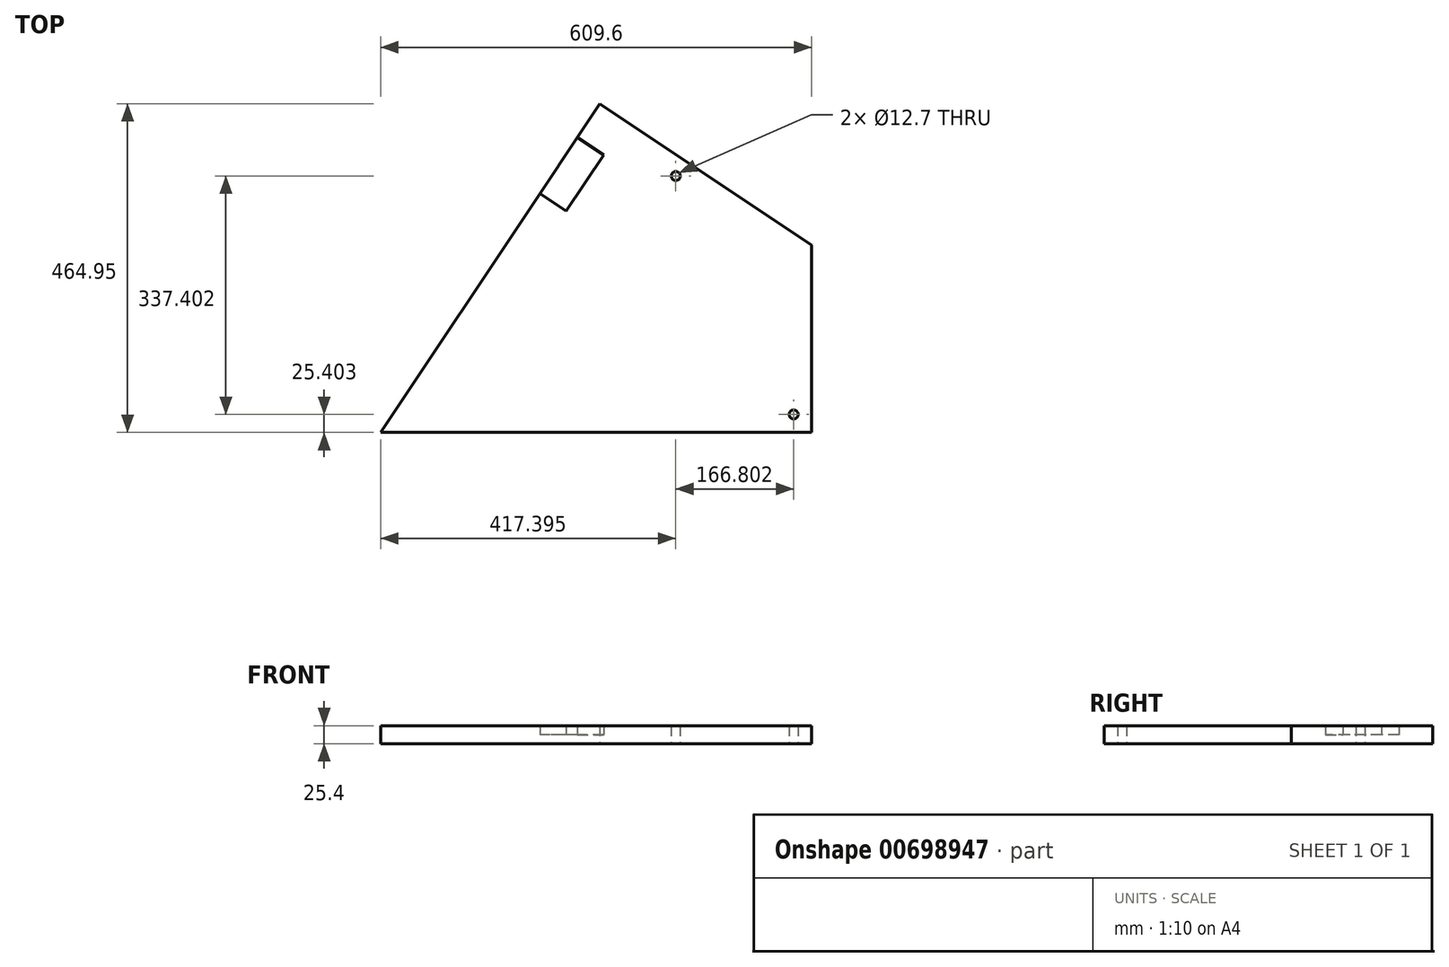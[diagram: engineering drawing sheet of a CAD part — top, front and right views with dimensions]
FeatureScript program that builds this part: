
annotation { "Feature Type Name" : "Feature", "Feature Type Description" : "" }
export const myFeature = defineFeature(function(context is Context, id is Id, definition is map)
    precondition{}
    {
        {
            var Q0;
            Q0=qCreatedBy(makeId("Top.planeOp"),FACE);
            var sketch = newSketch(context, id + "F0", { "sketchPlane" : qUnion([Q0])});
            skLineSegment(sketch, "E0", {"start": v(-491.1, -175.83) * mm, "end": v(118.5, -175.83) * mm});
            skLineSegment(sketch, "E1", {"start": v(-181.13, 289.12) * mm, "end": v(-491.1, -175.83) * mm});
            skCircle(sketch, "E2", {"center": v(93.1, -150.43) * mm, "radius": 6.35 * mm});
            skCircle(sketch, "E3", {"center": v(-73.7, 186.97) * mm, "radius": 6.35 * mm});
            skLineSegment(sketch, "E4", {"start": v(-212.83, 241.57) * mm, "end": v(-175.84, 216.91) * mm});
            skLineSegment(sketch, "E5", {"start": v(-175.84, 216.91) * mm, "end": v(-228.68, 137.66) * mm});
            skLineSegment(sketch, "E6", {"start": v(-228.68, 137.66) * mm, "end": v(-265.66, 162.32) * mm});
            skLineSegment(sketch, "E7", {"start": v(-265.66, 162.32) * mm, "end": v(-212.83, 241.57) * mm});
            skLineSegment(sketch, "E8", {"start": v(-181.13, 289.12) * mm, "end": v(118.5, 89.37) * mm});
            skLineSegment(sketch, "E9", {"start": v(118.5, 89.37) * mm, "end": v(118.5, -175.83) * mm});
            skSolve(sketch);
        }
        {
            var Q0;
            {var subQ1=sQuery(id+"F0.wireOp",EDGE,"E0");Q0=makeQuery(id+"F0.imprint","IMPRINT",FACE,{"disambiguationData":[TD([[makeQuery(id+"F0.imprint","IMPRINT",EDGE,{"derivedFrom":subQ1}),1.0]])]});}
            extrude(context, id + "F1", {"entities" : qUnion([Q0]), "depth" : 25.4 * mm, "offsetDistance" : 25.4 * mm});
        }
        {
            var Q0;
            Q0 = qSketchRegion(id + "F0", true);
            extrude(context, id + "F2", {"entities" : qUnion([Q0]), "operationType" : NewBodyOperationType.ADD, "depth" : 12.7 * mm, "offsetDistance" : 25.4 * mm});
        }
    });
